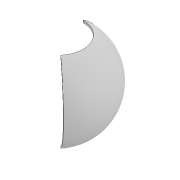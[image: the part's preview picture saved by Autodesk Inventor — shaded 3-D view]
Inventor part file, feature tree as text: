
AUTODESK INVENTOR PART (.ipt)
format: ipt  version: 2022 (Build 260153000, 153)  size: 128,000 bytes
history: native  units: mm
features: sketch x2, revolve x1, extrude x1
ambient origin geometry x8: Origin, YZ Plane, XZ Plane, XY Plane, X Axis, Y Axis, Z Axis, Center Point
bodies: Solid1 (feature_tree)
feature tree (4):
  revolve  "Revolution1"  [1 undecoded]
  extrude  "Extrusion1"  Depth=50.0mm
  sketch  "Sketch2"  dims[d8=2.0mm d9=45.0mm]
  sketch  "Sketch3"  dims[d11=22.68928mm d12=50.0mm d13=100.0mm d14=0.0mm]
note: 1 required parameter value undecoded (feature->parameter linkage not recoverable at this tier; creation-order binding heuristic only, values carry confidence <= 0.55)
